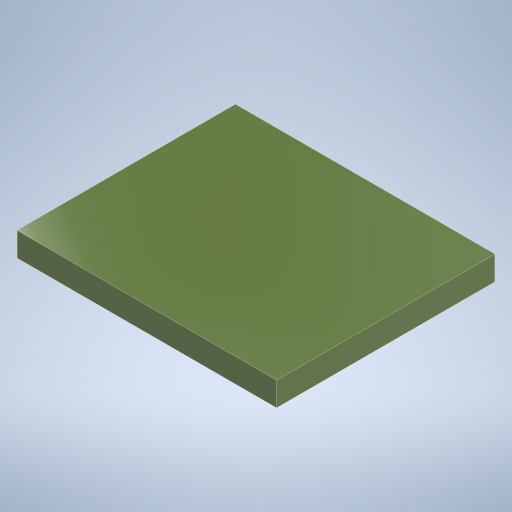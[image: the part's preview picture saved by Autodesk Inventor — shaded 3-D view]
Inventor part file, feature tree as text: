
AUTODESK INVENTOR PART (.ipt)
format: ipt  version: 2023 (Build 270158000, 158)  size: 208,384 bytes
history: native  units: in
note: dims shown in document units (in); Inventor stores cm internally (conversion verified against a paired STEP export)
features: extrude x1, sketch x1
ambient origin geometry x8: Origin, YZ Plane, XZ Plane, XY Plane, X Axis, Y Axis, Z Axis, Center Point
bodies: Solid1 (feature_tree)
feature tree (2):
  extrude  "Extrusion1"  Depth=0.0725in TaperAngle=0.0deg
  sketch  "Sketch1"  dims[d0=0.785in d1=0.0725in d2=0.0in]
